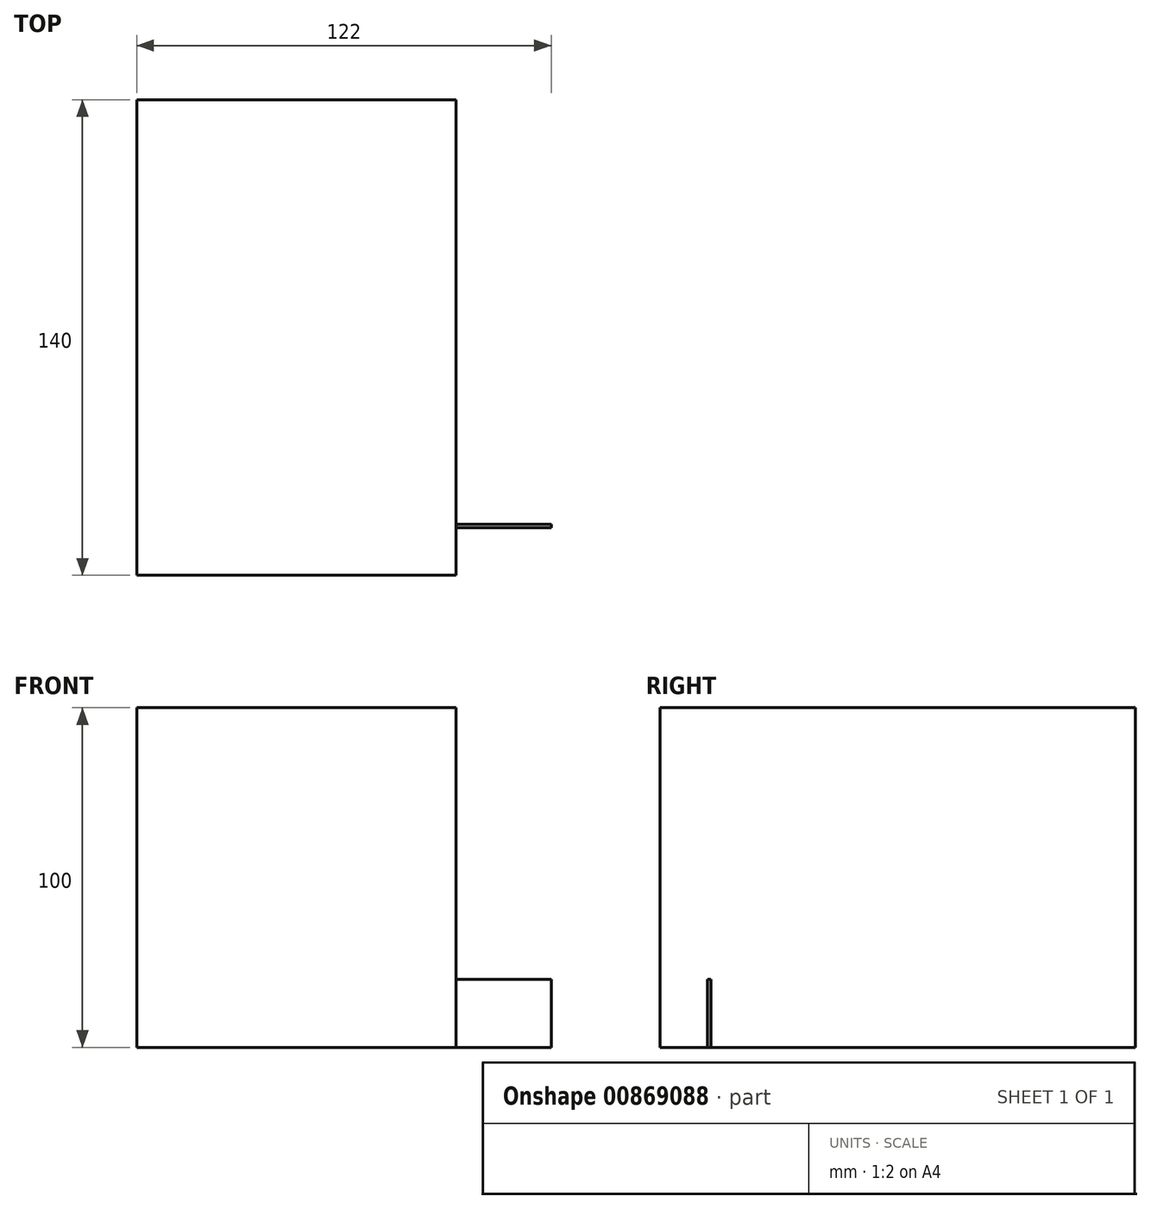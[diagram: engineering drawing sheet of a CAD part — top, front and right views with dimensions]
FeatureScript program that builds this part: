
annotation { "Feature Type Name" : "Feature", "Feature Type Description" : "" }
export const myFeature = defineFeature(function(context is Context, id is Id, definition is map)
    precondition{}
    {
        {
            var Q0;
            Q0=qCreatedBy(makeId("Top.planeOp"),FACE);
            var sketch = newSketch(context, id + "F0", { "sketchPlane" : qUnion([Q0])});
            skLineSegment(sketch, "E0", {"start": v(-28, 32) * mm, "end": v(-28, -55) * mm});
            skLineSegment(sketch, "E1", {"start": v(-28, -55) * mm, "end": v(122, -55) * mm});
            skLineSegment(sketch, "E2", {"start": v(122, -55) * mm, "end": v(122, 14) * mm});
            skLineSegment(sketch, "E3", {"start": v(122, 14) * mm, "end": v(94, 14) * mm});
            skLineSegment(sketch, "E4", {"start": v(94, 14) * mm, "end": v(94, 0) * mm});
            skLineSegment(sketch, "E5", {"start": v(94, 0) * mm, "end": v(0, 0) * mm});
            skLineSegment(sketch, "E6", {"start": v(0, 0) * mm, "end": v(0, 32) * mm});
            skLineSegment(sketch, "E7", {"start": v(0, 32) * mm, "end": v(-28, 32) * mm});
            skLineSegment(sketch, "E8", {"start": v(-28, -55) * mm, "end": v(-28, -60) * mm});
            skLineSegment(sketch, "E9", {"start": v(-28, -60) * mm, "end": v(122, -60) * mm});
            skLineSegment(sketch, "E10", {"start": v(122, -60) * mm, "end": v(122, -55) * mm});
            skLineSegment(sketch, "E11.bottom", {"start": v(-28, 32) * mm, "end": v(0, 32) * mm});
            skLineSegment(sketch, "E11.top", {"start": v(-28, 47) * mm, "end": v(0, 47) * mm});
            skLineSegment(sketch, "E11.left", {"start": v(-28, 32) * mm, "end": v(-28, 47) * mm});
            skLineSegment(sketch, "E11.right", {"start": v(0, 32) * mm, "end": v(0, 47) * mm});
            skLineSegment(sketch, "E12", {"start": v(-28, 44.04) * mm, "end": v(0, 44.04) * mm});
            skLineSegment(sketch, "E13", {"start": v(-28, 41.07) * mm, "end": v(0, 41.07) * mm});
            skLineSegment(sketch, "E14", {"start": v(-28, 35.06) * mm, "end": v(0, 35.06) * mm});
            skLineSegment(sketch, "E15", {"start": v(-28, 38.03) * mm, "end": v(0, 38.03) * mm});
            skLineSegment(sketch, "E16", {"start": v(0, 0) * mm, "end": v(0, -5) * mm});
            skLineSegment(sketch, "E17", {"start": v(0, -5) * mm, "end": v(99, -5) * mm});
            skLineSegment(sketch, "E18", {"start": v(99, -5) * mm, "end": v(99, 14) * mm});
            skPoint(sketch, "E19", {"position": v(0, 39.5) * mm});
            skLineSegment(sketch, "E20", {"start": v(122, -60) * mm, "end": v(204.72, -60) * mm});
            skLineSegment(sketch, "E21", {"start": v(-28, -60) * mm, "end": v(-110.72, -60) * mm});
            skLineSegment(sketch, "E22", {"start": v(-110.72, -100) * mm, "end": v(204.72, -100) * mm});
            skSolve(sketch);
        }
        {
            var Q0;
            Q0=qCreatedBy(makeId("Top.planeOp"),FACE);
            var sketch = newSketch(context, id + "F1", { "sketchPlane" : qUnion([Q0])});
            skLineSegment(sketch, "E23", {"start": v(0, 140) * mm, "end": v(0, 0) * mm});
            skLineSegment(sketch, "E24", {"start": v(0, 0) * mm, "end": v(94, 0) * mm});
            skLineSegment(sketch, "E25", {"start": v(94, 0) * mm, "end": v(94, 140) * mm});
            skLineSegment(sketch, "E26", {"start": v(94, 140) * mm, "end": v(0, 140) * mm});
            skSolve(sketch);
        }
        {
            var Q0;
            Q0 = qSketchRegion(id + "F1", true);
            extrude(context, id + "F2", {"entities" : qUnion([Q0]), "depth" : 100 * mm, "offsetDistance" : 25 * mm});
        }
        {
            var Q0;
            Q0=qCreatedBy(makeId("Top.planeOp"),FACE);
            var sketch = newSketch(context, id + "F3", { "sketchPlane" : qUnion([Q0])});
            skLineSegment(sketch, "E27.bottom", {"start": v(94, 15) * mm, "end": v(122, 15) * mm});
            skLineSegment(sketch, "E27.top", {"start": v(94, 14) * mm, "end": v(122, 14) * mm});
            skLineSegment(sketch, "E27.left", {"start": v(94, 15) * mm, "end": v(94, 14) * mm});
            skLineSegment(sketch, "E27.right", {"start": v(122, 15) * mm, "end": v(122, 14) * mm});
            skSolve(sketch);
        }
        {
            var Q0;
            Q0 = qSketchRegion(id + "F3", true);
            extrude(context, id + "F4", {"entities" : qUnion([Q0]), "operationType" : NewBodyOperationType.ADD, "depth" : 20 * mm, "offsetDistance" : 25 * mm});
        }
    });
